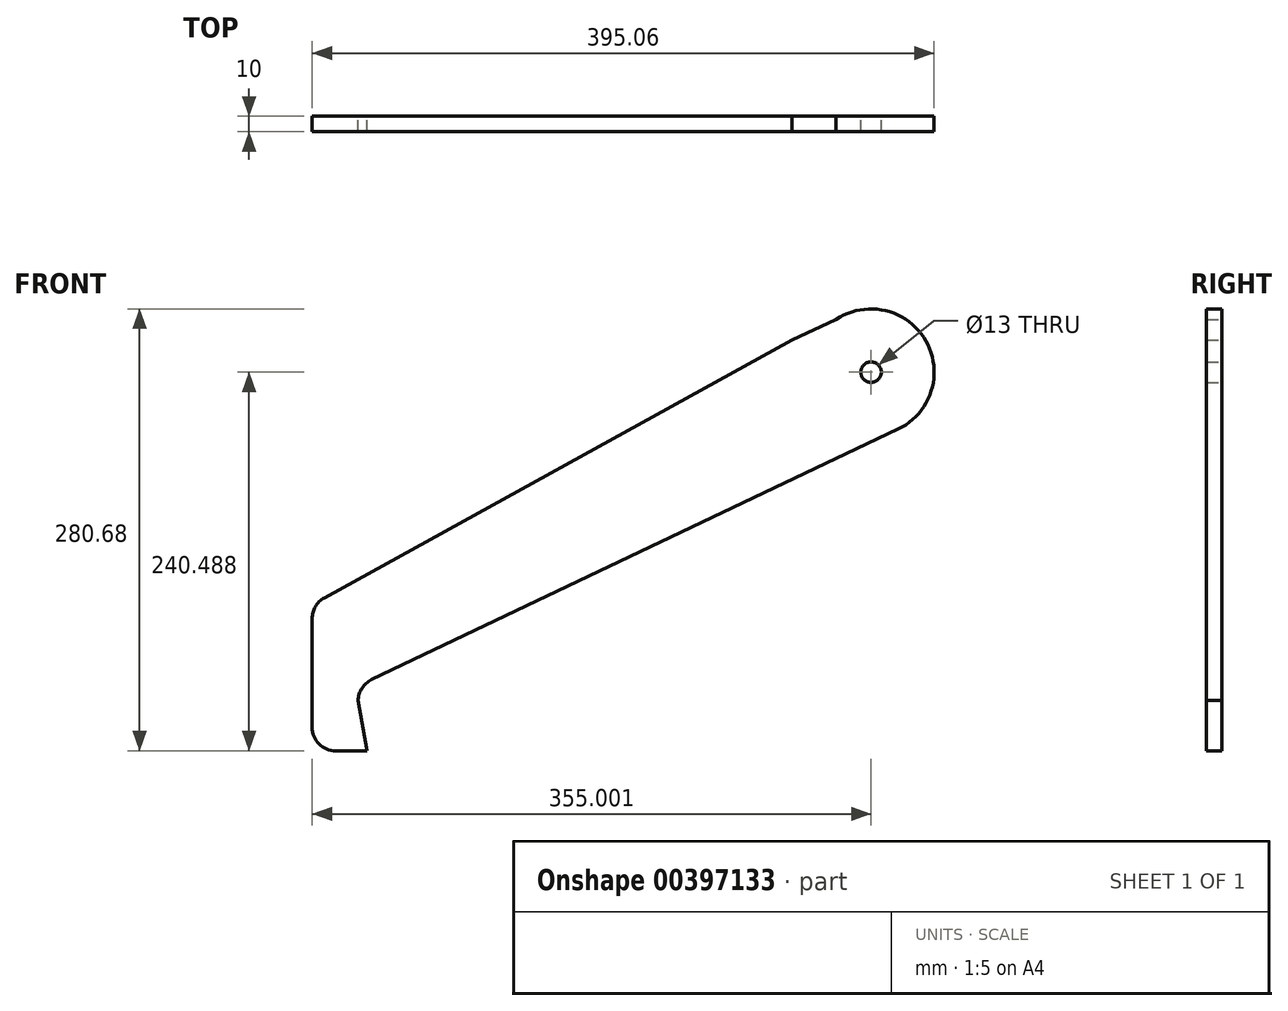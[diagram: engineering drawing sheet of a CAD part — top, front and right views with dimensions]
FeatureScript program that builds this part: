
annotation { "Feature Type Name" : "Feature", "Feature Type Description" : "" }
export const myFeature = defineFeature(function(context is Context, id is Id, definition is map)
    precondition{}
    {
        {
            var Q0;
            Q0=qCreatedBy(makeId("Front.planeOp"),FACE);
            var sketch = newSketch(context, id + "F0", { "sketchPlane" : qUnion([Q0])});
            skLineSegment(sketch, "E0.left", {"start": v(106.78, 41.03) * mm, "end": v(101.93, 45.36) * mm, "construction": true});
            skPoint(sketch, "E0.middle", {"position": v(-86.21, -41.62) * mm});
            skLineSegment(sketch, "E1", {"start": v(-245.31, -97.98) * mm, "end": v(51.77, 65.78) * mm});
            skLineSegment(sketch, "E2", {"start": v(-215.26, -149.92) * mm, "end": v(119.12, 9.24) * mm});
            skLineSegment(sketch, "E3", {"start": v(-253.07, -111.12) * mm, "end": v(-253.07, -180.13) * mm});
            skLineSegment(sketch, "E4", {"start": v(-238.07, -195.13) * mm, "end": v(-228.27, -195.13) * mm});
            skCircle(sketch, "E5", {"center": v(101.93, 45.36) * mm, "radius": 6.5 * mm});
            skArc(sketch, "E6.filletArc", {"start": v(-245.31, -97.98) * mm, "mid": v(-250.98, -103.5) * mm, "end": v(-253.07, -111.12) * mm});
            skArc(sketch, "E7.filletArc", {"start": v(-215.26, -149.92) * mm, "mid": v(-221.44, -155.36) * mm, "end": v(-223.81, -163.25) * mm});
            skArc(sketch, "E8.filletArc", {"start": v(-253.07, -180.13) * mm, "mid": v(-248.68, -190.74) * mm, "end": v(-238.07, -195.13) * mm});
            skLineSegment(sketch, "E9", {"start": v(101.93, 45.36) * mm, "end": v(101.93, -295.77) * mm, "construction": true});
            skLineSegment(sketch, "E10", {"start": v(-223.81, -163.25) * mm, "end": v(-218.07, -195.13) * mm});
            skLineSegment(sketch, "E11", {"start": v(-218.07, -195.13) * mm, "end": v(-228.27, -195.13) * mm});
            skPoint(sketch, "E12.orphan", {"position": v(240.74, 221.97) * mm});
            skPoint(sketch, "E13.orphan", {"position": v(129.55, 20.73) * mm});
            skPoint(sketch, "E14.orphan", {"position": v(74.32, 69.99) * mm});
            skLineSegment(sketch, "E15", {"start": v(101.93, 45.36) * mm, "end": v(119.12, 9.24) * mm, "construction": true});
            skLineSegment(sketch, "E16", {"start": v(101.93, 45.36) * mm, "end": v(79.7, 78.85) * mm, "construction": true});
            skArc(sketch, "E17", {"start": v(119.12, 9.24) * mm, "mid": v(136.78, 65.21) * mm, "end": v(79.7, 78.85) * mm});
            skPoint(sketch, "E18.orphan", {"position": v(131.39, 15.08) * mm});
            skPoint(sketch, "E19.orphan", {"position": v(-246.74, -153.23) * mm});
            skLineSegment(sketch, "E20", {"start": v(79.7, 78.85) * mm, "end": v(51.77, 65.78) * mm});
            skSolve(sketch);
        }
        {
            var Q0;
            Q0 = qSketchRegion(id + "F0", true);
            extrude(context, id + "F1", {"entities" : qUnion([Q0]), "depth" : 10 * mm, "offsetDistance" : 25 * mm});
        }
    });
